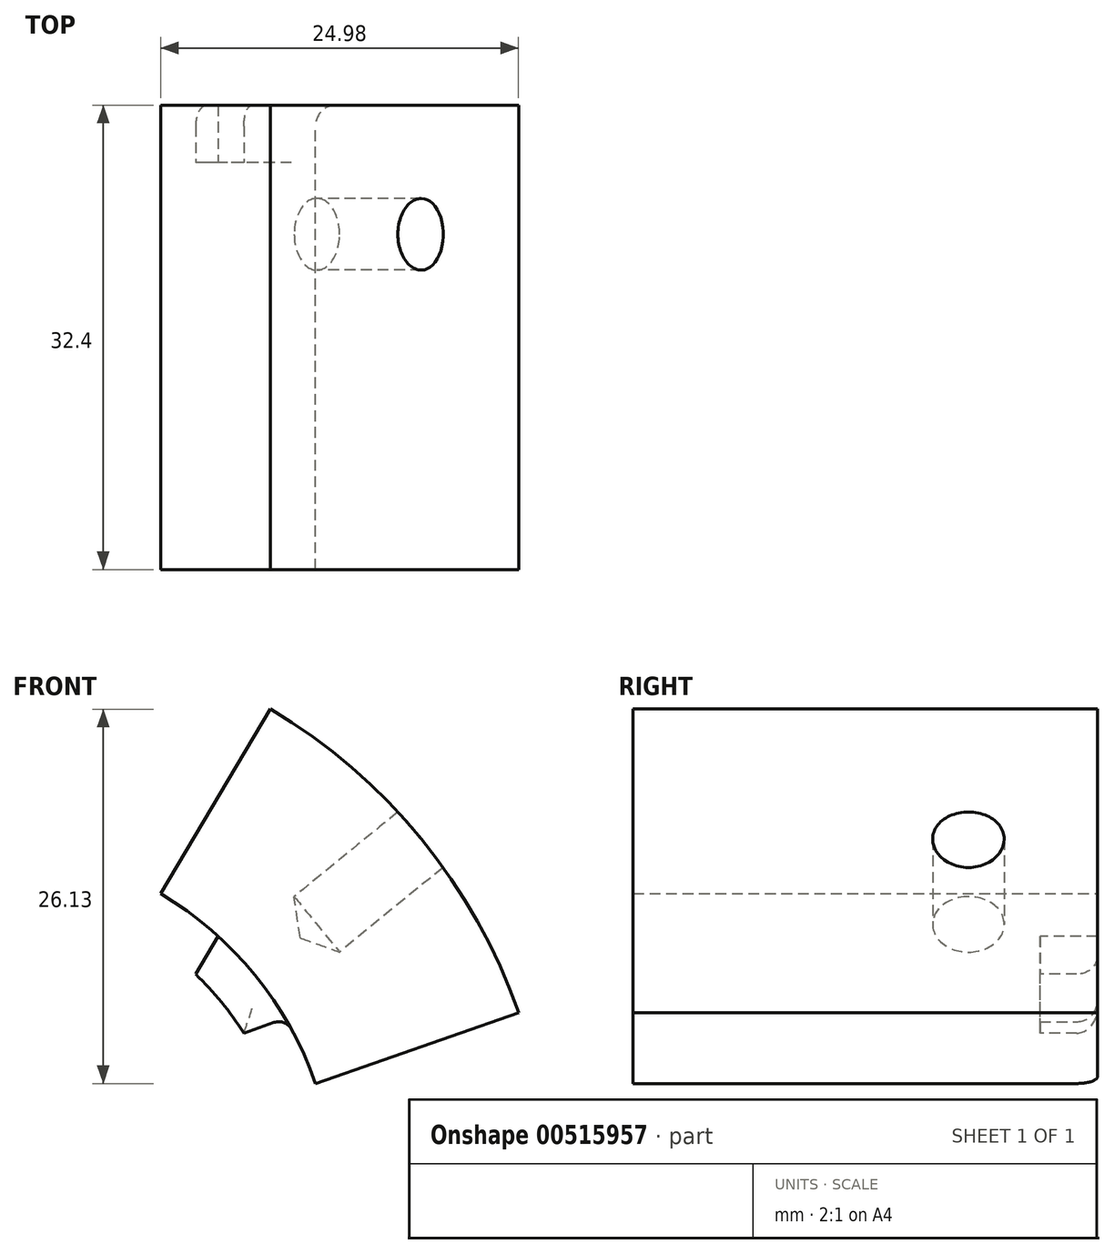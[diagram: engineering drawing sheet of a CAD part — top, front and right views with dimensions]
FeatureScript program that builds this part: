
annotation { "Feature Type Name" : "Feature", "Feature Type Description" : "" }
export const myFeature = defineFeature(function(context is Context, id is Id, definition is map)
    precondition{}
    {
        {
            var Q0;
            Q0=qCreatedBy(makeId("Front.planeOp"),FACE);
            var sketch = newSketch(context, id + "F0", { "sketchPlane" : qUnion([Q0])});
            skArc(sketch, "E0", {"start": v(37.76, 13.18) * mm, "mid": v(30.98, 25.3) * mm, "end": v(20.45, 34.37) * mm});
            skArc(sketch, "E1", {"start": v(23.6, 8.24) * mm, "mid": v(19.36, 15.82) * mm, "end": v(12.78, 21.48) * mm});
            skLineSegment(sketch, "E2", {"start": v(12.78, 21.48) * mm, "end": v(20.45, 34.37) * mm});
            skLineSegment(sketch, "E3", {"start": v(23.6, 8.24) * mm, "end": v(37.76, 13.18) * mm});
            skSolve(sketch);
        }
        {
            var Q0;
            Q0=qCreatedBy(makeId("Front.planeOp"),FACE);
            var sketch = newSketch(context, id + "F1", { "sketchPlane" : qUnion([Q0])});
            skArc(sketch, "E4", {"start": v(18.6, 11.76) * mm, "mid": v(17.04, 13.92) * mm, "end": v(15.23, 15.87) * mm});
            skLineSegment(sketch, "E5", {"start": v(20.5, 34.46) * mm, "end": v(12.78, 21.48) * mm});
            skLineSegment(sketch, "E6", {"start": v(37.76, 13.18) * mm, "end": v(23.6, 8.24) * mm});
            skArc(sketch, "E7", {"start": v(37.76, 13.18) * mm, "mid": v(30.98, 25.3) * mm, "end": v(20.45, 34.37) * mm});
            skArc(sketch, "E8", {"start": v(23.6, 8.24) * mm, "mid": v(22.66, 10.56) * mm, "end": v(21.5, 12.77) * mm});
            skLineSegment(sketch, "E9", {"start": v(21.5, 12.77) * mm, "end": v(18.6, 11.76) * mm});
            skLineSegment(sketch, "E10", {"start": v(16.8, 18.51) * mm, "end": v(15.23, 15.87) * mm});
            skArc(sketch, "E11.trimOffspring", {"start": v(16.8, 18.51) * mm, "mid": v(14.87, 20.1) * mm, "end": v(12.78, 21.48) * mm});
            skSolve(sketch);
        }
        {
            var Q0;
            Q0=makeQuery(id+"F0.imprint","IMPRINT",FACE,{"disambiguationData":[TD([[makeQuery(id+"F0.imprint","IMPRINT",EDGE,{"derivedFrom":sQuery(id+"F0.wireOp",EDGE,"E0")}),1.0]])]});
            extrude(context, id + "F2", {"entities" : qUnion([Q0]), "depth" : 28.4 * mm, "offsetDistance" : 25 * mm});
        }
        {
            var Q0;
            Q0=qSketchRegion(id+"F1",true);
            var Q1;
            Q1=qSketchRegion(id+"F0",true);
            extrude(context, id + "F3", {"entities" : qUnion([Q0, Q1]), "operationType" : NewBodyOperationType.ADD, "oppositeDirection" : true, "depth" : 4 * mm, "offsetDistance" : 25 * mm});
        }
        {
            var Q0;
            Q0=makeQuery(id+"F2.opExtrude","CAP_VERTEX",VERTEX,{"disambiguationData":[OSD([sQuery(id+"F0.wireOp",EDGE,"E0"),sQuery(id+"F0.wireOp",EDGE,"E3")])],"isStart":false});
            var Q1;
            Q1=makeQuery(id+"F2.opExtrude","CAP_VERTEX",VERTEX,{"disambiguationData":[OSD([sQuery(id+"F0.wireOp",EDGE,"E0"),sQuery(id+"F0.wireOp",EDGE,"E2")])],"isStart":false});
            var Q2;
            Q2=sQuery(id+"F0.wireOp",VERTEX,"E2.end");
            cPlane(context, id + "F4", {"entities" : qUnion([Q0, Q1, Q2]), "cplaneType" : CPlaneType.THREE_POINT, "offset" : 0 * mm, "width" : 150 * mm, "height" : 150 * mm});
        }
        {
            var Q0;
            Q0=qCreatedBy(id+"F4.planeOp",FACE);
            var sketch = newSketch(context, id + "F5", { "sketchPlane" : qUnion([Q0])});
            skCircle(sketch, "E12", {"center": v(-5, 0) * mm, "radius": 2.5 * mm});
            skSolve(sketch);
        }
        {
            var Q0;
            Q0=sQuery(id+"F5.wireOp",VERTEX,"E12.center");
            var Q1;
            Q1=makeQuery(id+"F2.opExtrude","SWEPT_BODY",BODY,{"disambiguationData":[OSD([sQuery(id+"F0.wireOp",EDGE,"E0"),sQuery(id+"F0.wireOp",EDGE,"E1"),sQuery(id+"F0.wireOp",EDGE,"E2"),sQuery(id+"F0.wireOp",EDGE,"E3")])]});
            hole(context, id + "F6", {"style" : HoleStyle.SIMPLE, "endStyle" : HoleEndStyle.BLIND, "oppositeDirection" : true, "holeDiameter" : 5 * mm, "holeDepth" : 5 * mm, "isTappedThrough" : true, "tappedDepth" : 12 * mm, "tapClearance" : 3, "startFromSketch" : true, "locations" : qUnion([Q0]), "scope" : qUnion([Q1])});
        }
        {
            var Q0;
            Q0=sQuery(id+"F5.wireOp",VERTEX,"E12.center");
            var Q1;
            Q1=makeQuery(id+"F2.opExtrude","SWEPT_BODY",BODY,{"disambiguationData":[OSD([sQuery(id+"F0.wireOp",EDGE,"E0"),sQuery(id+"F0.wireOp",EDGE,"E1"),sQuery(id+"F0.wireOp",EDGE,"E2"),sQuery(id+"F0.wireOp",EDGE,"E3")])]});
            hole(context, id + "F7", {"style" : HoleStyle.SIMPLE, "endStyle" : HoleEndStyle.BLIND, "holeDiameter" : 5 * mm, "holeDepth" : 7 * mm, "isTappedThrough" : true, "tappedDepth" : 12 * mm, "tapClearance" : 3, "startFromSketch" : true, "locations" : qUnion([Q0]), "scope" : qUnion([Q1])});
        }
        {
            var Q0;
            Q0=makeQuery(id+"F3.opExtrude","SWEPT_EDGE",EDGE,{"disambiguationData":[OSD([sQuery(id+"F1.wireOp",EDGE,"E8"),sQuery(id+"F1.wireOp",EDGE,"E9")])]});
            var Q1;
            Q1=makeQuery(id+"F3.opExtrude","SWEPT_EDGE",EDGE,{"disambiguationData":[OSD([sQuery(id+"F1.wireOp",EDGE,"E10"),sQuery(id+"F1.wireOp",EDGE,"E11.trimOffspring")])]});
            fillet(context, id + "F8", {"entities" : qUnion([Q0, Q1]), "radius" : 1 * mm, "tangentPropagation" : true, "allowEdgeOverflow" : false});
        }
        {
            var Q0;
            Q0=makeQuery(id+"F3.opExtrude","CAP_EDGE",EDGE,{"disambiguationData":[OSD([sQuery(id+"F1.wireOp",EDGE,"E4")])],"isStart":false});
            var Q1;
            {var subQ0=sQuery(id+"F1.wireOp",EDGE,"E11.trimOffspring");var subQ1=sQuery(id+"F1.wireOp",EDGE,"E10");Q1=makeQuery(id+"F8.opFillet","BLEND_EDGE",EDGE,{"blendedFrom":[makeQuery(id+"F3.opExtrude","SWEPT_EDGE",EDGE,{"disambiguationData":[OSD([subQ1,subQ0])]}),makeQuery(id+"F3.boolean.opBoolean","MERGE",FACE,{"derivedFrom":[makeQuery(id+"F3.opExtrude","CAP_FACE",FACE,{"disambiguationData":[OSD([sQuery(id+"F0.wireOp",EDGE,"E0"),sQuery(id+"F0.wireOp",EDGE,"E1"),sQuery(id+"F0.wireOp",EDGE,"E2"),sQuery(id+"F0.wireOp",EDGE,"E3")])],"isStart":false}),makeQuery(id+"F3.opExtrude","CAP_FACE",FACE,{"disambiguationData":[OSD([sQuery(id+"F1.wireOp",EDGE,"E4"),sQuery(id+"F1.wireOp",EDGE,"E5"),sQuery(id+"F1.wireOp",EDGE,"E6"),sQuery(id+"F1.wireOp",EDGE,"E7"),sQuery(id+"F1.wireOp",EDGE,"E8"),sQuery(id+"F1.wireOp",EDGE,"E9"),subQ1,subQ0])],"isStart":false})]})],"blendedInto":[makeQuery(id+"F3.boolean.opBoolean","MERGE",FACE,{"derivedFrom":[makeQuery(id+"F3.opExtrude","CAP_FACE",FACE,{"disambiguationData":[OSD([sQuery(id+"F0.wireOp",EDGE,"E0"),sQuery(id+"F0.wireOp",EDGE,"E1"),sQuery(id+"F0.wireOp",EDGE,"E2"),sQuery(id+"F0.wireOp",EDGE,"E3")])],"isStart":false}),makeQuery(id+"F3.opExtrude","CAP_FACE",FACE,{"disambiguationData":[OSD([sQuery(id+"F1.wireOp",EDGE,"E4"),sQuery(id+"F1.wireOp",EDGE,"E5"),sQuery(id+"F1.wireOp",EDGE,"E6"),sQuery(id+"F1.wireOp",EDGE,"E7"),sQuery(id+"F1.wireOp",EDGE,"E8"),sQuery(id+"F1.wireOp",EDGE,"E9"),subQ1,subQ0])],"isStart":false})]})]});}
            var Q2;
            {var subQ0=sQuery(id+"F1.wireOp",EDGE,"E9");var subQ1=sQuery(id+"F1.wireOp",EDGE,"E8");Q2=makeQuery(id+"F8.opFillet","BLEND_EDGE",EDGE,{"blendedFrom":[makeQuery(id+"F3.opExtrude","SWEPT_EDGE",EDGE,{"disambiguationData":[OSD([subQ1,subQ0])]}),makeQuery(id+"F3.boolean.opBoolean","MERGE",FACE,{"derivedFrom":[makeQuery(id+"F3.opExtrude","CAP_FACE",FACE,{"disambiguationData":[OSD([sQuery(id+"F0.wireOp",EDGE,"E0"),sQuery(id+"F0.wireOp",EDGE,"E1"),sQuery(id+"F0.wireOp",EDGE,"E2"),sQuery(id+"F0.wireOp",EDGE,"E3")])],"isStart":false}),makeQuery(id+"F3.opExtrude","CAP_FACE",FACE,{"disambiguationData":[OSD([sQuery(id+"F1.wireOp",EDGE,"E4"),sQuery(id+"F1.wireOp",EDGE,"E5"),sQuery(id+"F1.wireOp",EDGE,"E6"),sQuery(id+"F1.wireOp",EDGE,"E7"),subQ1,subQ0,sQuery(id+"F1.wireOp",EDGE,"E10"),sQuery(id+"F1.wireOp",EDGE,"E11.trimOffspring")])],"isStart":false})]})],"blendedInto":[makeQuery(id+"F3.boolean.opBoolean","MERGE",FACE,{"derivedFrom":[makeQuery(id+"F3.opExtrude","CAP_FACE",FACE,{"disambiguationData":[OSD([sQuery(id+"F0.wireOp",EDGE,"E0"),sQuery(id+"F0.wireOp",EDGE,"E1"),sQuery(id+"F0.wireOp",EDGE,"E2"),sQuery(id+"F0.wireOp",EDGE,"E3")])],"isStart":false}),makeQuery(id+"F3.opExtrude","CAP_FACE",FACE,{"disambiguationData":[OSD([sQuery(id+"F1.wireOp",EDGE,"E4"),sQuery(id+"F1.wireOp",EDGE,"E5"),sQuery(id+"F1.wireOp",EDGE,"E6"),sQuery(id+"F1.wireOp",EDGE,"E7"),subQ1,subQ0,sQuery(id+"F1.wireOp",EDGE,"E10"),sQuery(id+"F1.wireOp",EDGE,"E11.trimOffspring")])],"isStart":false})]})]});}
            fillet(context, id + "F9", {"entities" : qUnion([Q0, Q1, Q2]), "radius" : 1.45 * mm, "tangentPropagation" : true, "allowEdgeOverflow" : false});
        }
    });
